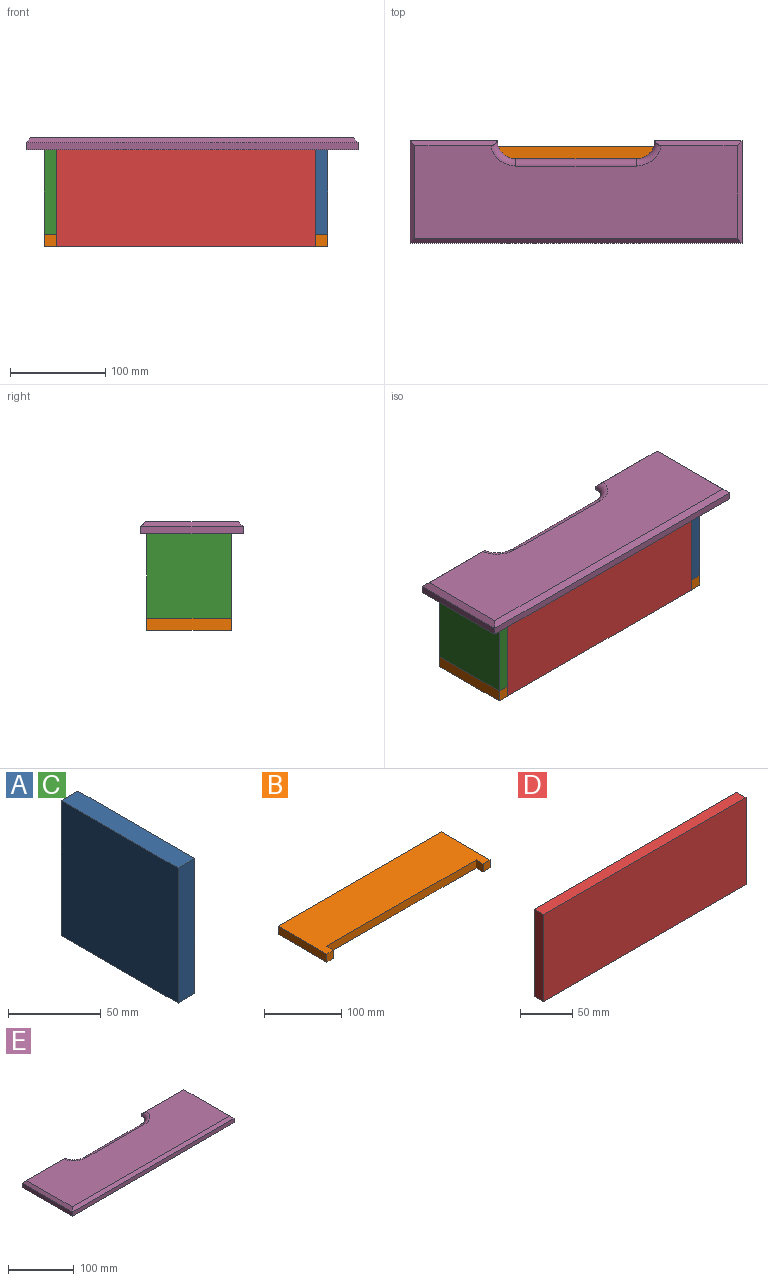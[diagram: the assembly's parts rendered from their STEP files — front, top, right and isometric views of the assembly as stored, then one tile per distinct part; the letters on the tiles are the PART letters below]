
ASSEMBLY  parts=5 mates=4
PART A: 6 faces, bbox 12.7x88.9x88.9 mm
  f0: plane 88.9x12.7mm, normal (0,0,-1), area 1129mm2, adj f1,f3,f4,f5
  f1: plane 88.9x12.7mm, normal (0,1,0), area 1129mm2, adj f0,f2,f4,f5
  f2: plane 88.9x12.7mm, normal (0,0,1), area 1129mm2, adj f1,f3,f4,f5
  f3: plane 88.9x12.7mm, normal (0,-1,0), area 1129mm2, adj f0,f2,f4,f5
  f4: plane 88.9x88.9mm, normal (1,0,0), area 7903.2mm2, adj f0,f1,f2,f3
  f5: plane 88.9x88.9mm, normal (-1,0,0), area 7903.2mm2, adj f0,f1,f2,f3
PART B: 10 faces, bbox 298.5x88.9x12.7 mm
  f0: plane 12.7x12.7mm, normal (1,0,0), area 161.3mm2, adj f1,f7,f8,f9
  f1: plane 273.05x12.7mm, normal (0,-1,0), area 3467.7mm2, adj f0,f2,f8,f9
  f2: plane 12.7x12.7mm, normal (-1,0,0), area 161.3mm2, adj f1,f3,f8,f9
  f3: plane 12.7x12.7mm, normal (0,-1,0), area 161.3mm2, adj f2,f4,f8,f9
  f4: plane 88.9x12.7mm, normal (1,0,0), area 1129mm2, adj f3,f5,f8,f9
  f5: plane 298.45x12.7mm, normal (0,1,0), area 3790.3mm2, adj f4,f6,f8,f9
  f6: plane 88.9x12.7mm, normal (-1,0,0), area 1129mm2, adj f5,f7,f8,f9
  f7: plane 12.7x12.7mm, normal (0,-1,0), area 161.3mm2, adj f0,f6,f8,f9
  f8: plane 298.45x88.9mm, normal (0,0,1), area 23064.5mm2, adj f0,f1,f2,f3,f4,f5,f6,f7
  f9: plane 298.45x88.9mm, normal (0,0,-1), area 23064.5mm2, adj f0,f1,f2,f3,f4,f5,f6,f7
PART C: same geometry as A
PART D: 6 faces, bbox 273.1x12.7x101.6 mm
  f0: plane 101.6x12.7mm, normal (-1,0,0), area 1290.3mm2, adj f1,f3,f4,f5
  f1: plane 273.05x12.7mm, normal (0,0,-1), area 3467.7mm2, adj f0,f2,f4,f5
  f2: plane 101.6x12.7mm, normal (1,0,0), area 1290.3mm2, adj f1,f3,f4,f5
  f3: plane 273.05x12.7mm, normal (0,0,1), area 3467.7mm2, adj f0,f2,f4,f5
  f4: plane 273.05x101.6mm, normal (0,-1,0), area 27741.9mm2, adj f0,f1,f2,f3
  f5: plane 273.05x101.6mm, normal (0,1,0), area 27741.9mm2, adj f0,f1,f2,f3
PART E: 18 faces, bbox 349.3x108x12.7 mm
  f0: plane 91.97x7.62mm, normal (0,1,0), area 688.9mm2, adj f4,f6,f7,f8,f17
  f1: plane 91.97x7.62mm, normal (0,1,0), area 688.9mm2, adj f2,f6,f11,f12,f13
  f2: plane 107.95x7.62mm, normal (-1,0,0), area 822.6mm2, adj f1,f3,f6,f14
  f3: plane 349.25x7.62mm, normal (0,-1,0), area 2661.3mm2, adj f2,f4,f6,f15
  f4: plane 107.95x7.62mm, normal (1,0,0), area 822.6mm2, adj f0,f3,f6,f16
  f5: plane 339.09x97.79mm, normal (0,0,1), area 29569.7mm2, adj f7,f9,f11,f13,f14,f15,f16,f17
  f6: plane 349.25x107.95mm, normal (0,0,-1), area 33197.2mm2, adj f0,f1,f2,f3,f4,f8,f10,f12
  f7: torus R=26.67mm, axis (0,0,1), area 340.9mm2, adj f0,f5,f8,f9,f17
  f8: torus R=26.67mm, axis (0,0,1), area 372mm2, adj f0,f6,f7,f10
  f9: cylinder r=7.62mm len=127mm, axis (1,0,0), area 1358.1mm2, adj f5,f7,f10,f11
  f10: cylinder r=7.62mm len=127mm, axis (-1,0,0), area 1358.1mm2, adj f6,f8,f9,f12
  f11: torus R=26.67mm, axis (0,0,1), area 340.9mm2, adj f1,f5,f9,f12,f13
  f12: torus R=26.67mm, axis (0,0,1), area 372mm2, adj f1,f6,f10,f11
  f13: plane 91.64x5.08mm, normal (0,0.71,0.71), area 627.5mm2, adj f1,f5,f11,f14
  f14: plane 107.95x5.08mm, normal (-0.71,0,0.71), area 739mm2, adj f2,f5,f13,f15
  f15: plane 349.25x5.08mm, normal (0,-0.71,0.71), area 2472.6mm2, adj f3,f5,f14,f16
  f16: plane 107.95x5.08mm, normal (0.71,0,0.71), area 739mm2, adj f4,f5,f15,f17
  f17: plane 91.64x5.08mm, normal (0,0.71,0.71), area 627.5mm2, adj f0,f5,f7,f16
PLACE A t=(194.34,-190.04,64.79)mm
PLACE B t=(45.1,-375.91,-101.6)mm
PLACE C t=(-91.41,-190.04,64.79)mm
PLACE D t=(54.84,-290.49,-101.26)mm
PLACE E t=(-6.35,0,0)mm
MATE fastened B.f2 <-> D.f2  axis (-1,0,0) through (194.34,-303.19,-101.6)mm
MATE fastened C.f0 <-> B.f8  axis (0,0,-1) through (-91.41,-303.19,-88.9)mm
MATE fastened D.f3 <-> E.f6  axis (0,0,1) through (57.81,-303.19,0)mm
MATE fastened A.f0 <-> B.f8  axis (0,0,-1) through (207.04,-303.19,-88.9)mm
